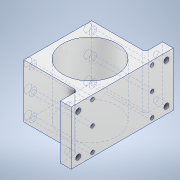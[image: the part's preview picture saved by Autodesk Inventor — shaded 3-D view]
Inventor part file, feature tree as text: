
AUTODESK INVENTOR PART (.ipt)
format: ipt  version: 2020.1 (Build 241239000, 239)  size: 180,224 bytes
history: native  units: mm
features: sketch x4, projected_geometry x3, extrude x2, other x1, fillet x1, hole x1
ambient origin geometry x8: Origin, YZ Plane, XZ Plane, XY Plane, X Axis, Y Axis, Z Axis, Center Point
bodies: Body1 (feature_tree)
feature tree (12):
  other  "Твердое тело1"
  extrude  "Выдавливание1"  Depth=100.0mm
  sketch  "Эскиз2"
  fillet  "Сопряжение1"  Radius=32.0mm
  extrude  "Выдавливание2"  Depth=32.0mm
  hole  "Отверстие1"  [1 undecoded]
  sketch  "Эскиз1"
  sketch  "Эскиз3"
  projected_geometry  "Спроецированная петля1"
  projected_geometry  "Спроецированная петля2"
  sketch  "Эскиз4"
  projected_geometry  "Спроецированная петля3"
note: 1 required parameter value undecoded (feature->parameter linkage not recoverable at this tier; creation-order binding heuristic only, values carry confidence <= 0.55)
